# Revit family: E18SW Loudspeaker
name_source: partatom
category: Communication Devices
revit_build: Autodesk Revit 2014 (Build: 20130308_1515(x64)
units: mm (PartAtom-declared; Revit-internal decimal feet)

## types (1)
- E18SW Loudspeaker
    Default Elevation = 0 mm
    Depth = 605 mm
    Description = 18" Passive Subwoofer
    Enclosure Material = Black Finish
    Grille Material = Black Grille
    Height = 616 mm
    Impedance = 4
    Manufacturer = QSC Audio Products, LLC
    Manufacturer URL = www.qsc.com
    Model = E18SW
    Power Handling = 800
    Power Handling 2 = 3200
    Product Documentation Link = http://www.qsc.com
    Product Page URL = http://www.qsc.com
    SPL Max = 132
    Sensitivity = 97
    URL = http://www.qsc.com
    Weight Dimensional (kg) = 48
    Weight Dimensional (lb) = 105
    Weight Product (kg) = 43
    Weight Product (lb) = 94
    Width = 590 mm

## geometry (parser evidence)
native form markers: Blend x1, Sweep x10
no freeform markers — native parametric forms only
